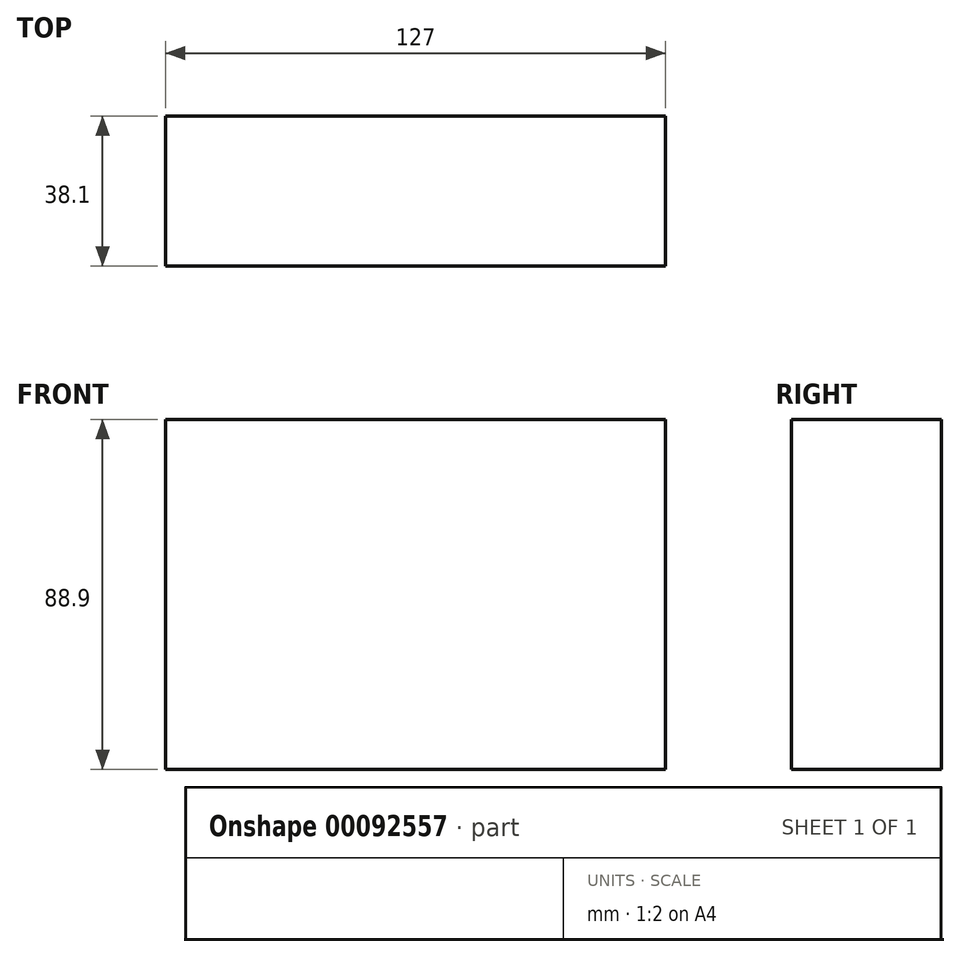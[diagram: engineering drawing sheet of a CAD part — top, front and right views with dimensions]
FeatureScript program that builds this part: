
annotation { "Feature Type Name" : "Feature", "Feature Type Description" : "" }
export const myFeature = defineFeature(function(context is Context, id is Id, definition is map)
    precondition{}
    {
        {
            var Q0;
            Q0=qCreatedBy(makeId("Front.planeOp"),FACE);
            var sketch = newSketch(context, id + "F0", { "sketchPlane" : qUnion([Q0])});
            skLineSegment(sketch, "E0.bottom", {"start": v(-105.95, 89.74) * mm, "end": v(21.05, 89.74) * mm});
            skLineSegment(sketch, "E0.top", {"start": v(-105.95, 0.84) * mm, "end": v(21.05, 0.84) * mm});
            skLineSegment(sketch, "E0.left", {"start": v(-105.95, 89.74) * mm, "end": v(-105.95, 0.84) * mm});
            skLineSegment(sketch, "E0.right", {"start": v(21.05, 89.74) * mm, "end": v(21.05, 0.84) * mm});
            skSolve(sketch);
        }
        {
            var Q0;
            Q0=makeQuery(id+"F0.imprint","IMPRINT",FACE,{"disambiguationData":[TD([[makeQuery(id+"F0.imprint","IMPRINT",EDGE,{"derivedFrom":sQuery(id+"F0.wireOp",EDGE,"E0.bottom")}),-1.0]])]});
            extrude(context, id + "F1", {"entities" : qUnion([Q0]), "depth" : 38.1 * mm});
        }
    });
